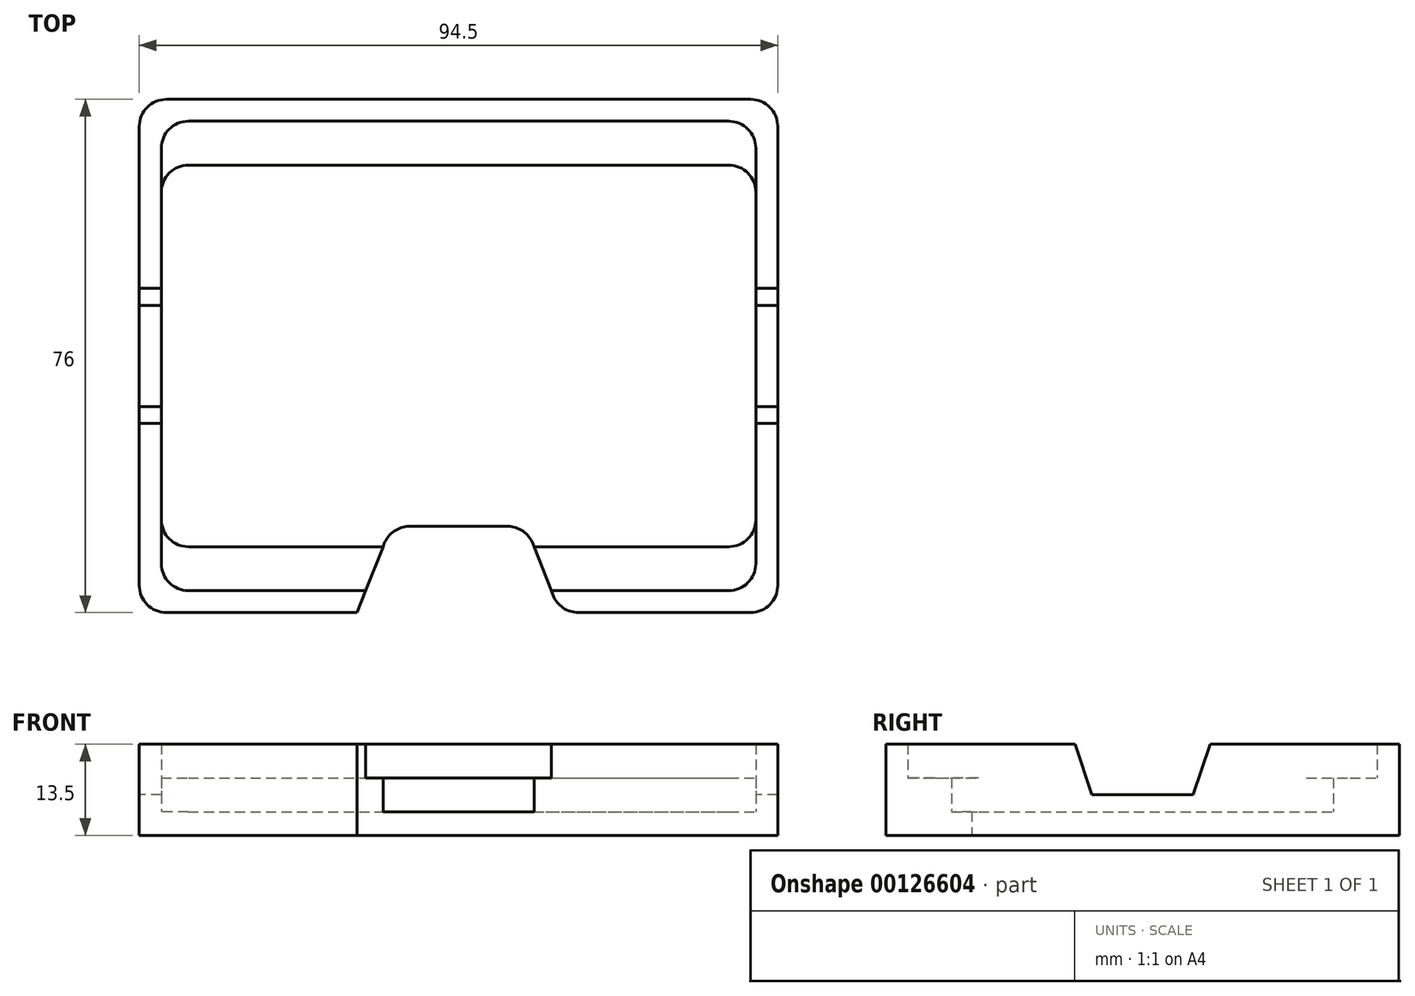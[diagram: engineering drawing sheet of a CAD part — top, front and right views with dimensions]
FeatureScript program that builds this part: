
annotation { "Feature Type Name" : "Feature", "Feature Type Description" : "" }
export const myFeature = defineFeature(function(context is Context, id is Id, definition is map)
    precondition{}
    {
        {
            var Q0;
            Q0=qCreatedBy(makeId("Top.planeOp"),FACE);
            var sketch = newSketch(context, id + "F0", { "sketchPlane" : qUnion([Q0])});
            skLineSegment(sketch, "E0.bottom", {"start": v(4, 0) * mm, "end": v(84, 0) * mm});
            skLineSegment(sketch, "E0.top", {"start": v(4, 56.5) * mm, "end": v(84, 56.5) * mm});
            skLineSegment(sketch, "E0.left", {"start": v(0, 4) * mm, "end": v(0, 52.5) * mm});
            skLineSegment(sketch, "E0.right", {"start": v(88, 4) * mm, "end": v(88, 52.5) * mm});
            skPoint(sketch, "E1.visualSharp", {"position": v(0, 56.5) * mm});
            skArc(sketch, "E1.filletArc", {"start": v(4, 56.5) * mm, "mid": v(1.17, 55.33) * mm, "end": v(0, 52.5) * mm});
            skPoint(sketch, "E2.visualSharp", {"position": v(88, 56.5) * mm});
            skArc(sketch, "E2.filletArc", {"start": v(88, 52.5) * mm, "mid": v(86.83, 55.33) * mm, "end": v(84, 56.5) * mm});
            skPoint(sketch, "E3.visualSharp", {"position": v(88, 0) * mm});
            skArc(sketch, "E3.filletArc", {"start": v(84, 0) * mm, "mid": v(86.83, 1.17) * mm, "end": v(88, 4) * mm});
            skPoint(sketch, "E4.visualSharp", {"position": v(0, 0) * mm});
            skArc(sketch, "E4.filletArc", {"start": v(0, 4) * mm, "mid": v(1.17, 1.17) * mm, "end": v(4, 0) * mm});
            skSolve(sketch);
        }
        {
            var Q0;
            Q0=qCreatedBy(makeId("Top.planeOp"),FACE);
            var sketch = newSketch(context, id + "F1", { "sketchPlane" : qUnion([Q0])});
            skLineSegment(sketch, "E5", {"start": v(0, 0) * mm, "end": v(0, -9.75) * mm, "construction": true});
            skLineSegment(sketch, "E6", {"start": v(0, -9.75) * mm, "end": v(-3.25, -9.75) * mm, "construction": true});
            skLineSegment(sketch, "E7.bottom", {"start": v(0.75, -9.75) * mm, "end": v(87.25, -9.75) * mm});
            skLineSegment(sketch, "E7.top", {"start": v(0.75, 66.25) * mm, "end": v(87.25, 66.25) * mm});
            skLineSegment(sketch, "E7.left", {"start": v(-3.25, -5.75) * mm, "end": v(-3.25, 62.25) * mm});
            skLineSegment(sketch, "E7.right", {"start": v(91.25, -5.75) * mm, "end": v(91.25, 62.25) * mm});
            skPoint(sketch, "E8.0", {"position": v(88, 56.5) * mm});
            skLineSegment(sketch, "E9", {"start": v(88, 56.5) * mm, "end": v(88, 66.25) * mm, "construction": true});
            skLineSegment(sketch, "E10", {"start": v(88, 66.25) * mm, "end": v(91.25, 66.25) * mm, "construction": true});
            skPoint(sketch, "E11.visualSharp", {"position": v(-3.25, 66.25) * mm});
            skArc(sketch, "E11.filletArc", {"start": v(0.75, 66.25) * mm, "mid": v(-2.08, 65.08) * mm, "end": v(-3.25, 62.25) * mm});
            skPoint(sketch, "E12.visualSharp", {"position": v(91.25, 66.25) * mm});
            skArc(sketch, "E12.filletArc", {"start": v(91.25, 62.25) * mm, "mid": v(90.08, 65.08) * mm, "end": v(87.25, 66.25) * mm});
            skPoint(sketch, "E13.visualSharp", {"position": v(91.25, -9.75) * mm});
            skArc(sketch, "E13.filletArc", {"start": v(87.25, -9.75) * mm, "mid": v(90.08, -8.58) * mm, "end": v(91.25, -5.75) * mm});
            skPoint(sketch, "E14.visualSharp", {"position": v(-3.25, -9.75) * mm});
            skArc(sketch, "E14.filletArc", {"start": v(-3.25, -5.75) * mm, "mid": v(-2.08, -8.58) * mm, "end": v(0.75, -9.75) * mm});
            skSolve(sketch);
        }
        {
            var Q0;
            Q0=makeQuery(id+"F1.imprint","IMPRINT",FACE,{"disambiguationData":[TD([[makeQuery(id+"F1.imprint","IMPRINT",EDGE,{"derivedFrom":sQuery(id+"F1.wireOp",EDGE,"E7.bottom")}),1.0]])]});
            extrude(context, id + "F2", {"entities" : qUnion([Q0]), "oppositeDirection" : true, "depth" : 3.5 * mm, "hasSecondDirection" : true, "secondDirectionOppositeDirection" : false, "secondDirectionDepth" : 10 * mm});
        }
        {
            var Q0;
            Q0=makeQuery(id+"F0.imprint","IMPRINT",FACE,{"disambiguationData":[TD([[makeQuery(id+"F0.imprint","IMPRINT",EDGE,{"derivedFrom":sQuery(id+"F0.wireOp",EDGE,"E0.bottom")}),1.0]])]});
            extrude(context, id + "F3", {"entities" : qUnion([Q0]), "operationType" : NewBodyOperationType.REMOVE, "depth" : 5 * mm});
        }
        {
            var Q0;
            Q0=qCreatedBy(makeId("Top.planeOp"),FACE);
            var sketch = newSketch(context, id + "F4", { "sketchPlane" : qUnion([Q0])});
            skLineSegment(sketch, "E15", {"start": v(0, 0) * mm, "end": v(0, -6.5) * mm, "construction": true});
            skLineSegment(sketch, "E16", {"start": v(88, 56.5) * mm, "end": v(88, 63) * mm, "construction": true});
            skLineSegment(sketch, "E17.bottom", {"start": v(4, -6.5) * mm, "end": v(84, -6.5) * mm});
            skLineSegment(sketch, "E17.top", {"start": v(4, 63) * mm, "end": v(84, 63) * mm});
            skLineSegment(sketch, "E17.left", {"start": v(0, -2.5) * mm, "end": v(0, 59) * mm});
            skLineSegment(sketch, "E17.right", {"start": v(88, -2.5) * mm, "end": v(88, 59) * mm});
            skPoint(sketch, "E18.visualSharp", {"position": v(0, 63) * mm});
            skArc(sketch, "E18.filletArc", {"start": v(4, 63) * mm, "mid": v(1.17, 61.83) * mm, "end": v(0, 59) * mm});
            skPoint(sketch, "E19.visualSharp", {"position": v(88, 63) * mm});
            skArc(sketch, "E19.filletArc", {"start": v(88, 59) * mm, "mid": v(86.83, 61.83) * mm, "end": v(84, 63) * mm});
            skPoint(sketch, "E20.visualSharp", {"position": v(88, -6.5) * mm});
            skArc(sketch, "E20.filletArc", {"start": v(84, -6.5) * mm, "mid": v(86.83, -5.33) * mm, "end": v(88, -2.5) * mm});
            skPoint(sketch, "E21.visualSharp", {"position": v(0, -6.5) * mm});
            skArc(sketch, "E21.filletArc", {"start": v(0, -2.5) * mm, "mid": v(1.17, -5.33) * mm, "end": v(4, -6.5) * mm});
            skSolve(sketch);
        }
        {
            var Q0;
            Q0=makeQuery(id+"F4.imprint","IMPRINT",FACE,{"disambiguationData":[TD([[makeQuery(id+"F4.imprint","IMPRINT",EDGE,{"derivedFrom":sQuery(id+"F4.wireOp",EDGE,"E17.bottom")}),1.0]])]});
            extrude(context, id + "F5", {"entities" : qUnion([Q0]), "operationType" : NewBodyOperationType.REMOVE, "depth" : 10 * mm, "hasSecondDirection" : true, "secondDirectionOppositeDirection" : false, "secondDirectionDepth" : 5 * mm});
        }
        {
            var Q0;
            Q0=qCreatedBy(makeId("Top.planeOp"),FACE);
            var sketch = newSketch(context, id + "F6", { "sketchPlane" : qUnion([Q0])});
            skLineSegment(sketch, "E22.0", {"start": v(0.75, -9.75) * mm, "end": v(87.25, -9.75) * mm});
            skLineSegment(sketch, "E23", {"start": v(44, -9.75) * mm, "end": v(44, 3) * mm, "construction": true});
            skLineSegment(sketch, "E24", {"start": v(44, 3) * mm, "end": v(51.27, 3) * mm});
            skLineSegment(sketch, "E25", {"start": v(44, -9.75) * mm, "end": v(59, -9.75) * mm});
            skLineSegment(sketch, "E26", {"start": v(55, 0.46) * mm, "end": v(59, -9.75) * mm});
            skLineSegment(sketch, "E27.MirrorCS", {"start": v(44, -9.75) * mm, "end": v(29, -9.75) * mm});
            skLineSegment(sketch, "E28.MirrorCS", {"start": v(44, 3) * mm, "end": v(36.73, 3) * mm});
            skLineSegment(sketch, "E29.MirrorCS", {"start": v(33, 0.46) * mm, "end": v(29, -9.75) * mm});
            skPoint(sketch, "E30.visualSharp", {"position": v(34, 3) * mm});
            skArc(sketch, "E30.filletArc", {"start": v(36.73, 3) * mm, "mid": v(34.47, 2.3) * mm, "end": v(33, 0.46) * mm});
            skPoint(sketch, "E31.visualSharp", {"position": v(54, 3) * mm});
            skArc(sketch, "E31.filletArc", {"start": v(55, 0.46) * mm, "mid": v(53.53, 2.3) * mm, "end": v(51.27, 3) * mm});
            skSolve(sketch);
        }
        {
            var Q0;
            Q0=makeQuery(id+"F6.imprint","IMPRINT",FACE,{"disambiguationData":[TD([[makeQuery(id+"F6.imprint","IMPRINT",EDGE,{"derivedFrom":sQuery(id+"F6.wireOp",EDGE,"E24")}),-1.0]])]});
            extrude(context, id + "F7", {"entities" : qUnion([Q0]), "operationType" : NewBodyOperationType.REMOVE, "depth" : 10 * mm, "hasSecondDirection" : true, "secondDirectionOppositeDirection" : true, "secondDirectionDepth" : 3.5 * mm});
        }
        {
            var Q0;
            Q0=makeQuery(id+"F7.boolean.opBoolean","COPY",EDGE,{"derivedFrom":makeQuery(id+"F7.opExtrude","SWEPT_EDGE",EDGE,{"disambiguationData":[OSD([sQuery(id+"F6.wireOp",EDGE,"E25"),sQuery(id+"F6.wireOp",EDGE,"E26")])]})});
            var Q1;
            Q1=makeQuery(id+"F7.boolean.opBoolean","COPY",EDGE,{"derivedFrom":makeQuery(id+"F7.opExtrude","SWEPT_EDGE",EDGE,{"disambiguationData":[OSD([sQuery(id+"F6.wireOp",EDGE,"E27.MirrorCS"),sQuery(id+"F6.wireOp",EDGE,"E29.MirrorCS")])]})});
            fillet(context, id + "F8", {"entities" : qUnion([Q0, Q1]), "radius" : 4 * mm, "tangentPropagation" : true, "allowEdgeOverflow" : false});
        }
        {
            var Q0;
            Q0=makeQuery(id+"F2.opExtrude","SWEPT_FACE",FACE,{"disambiguationData":[OSD([sQuery(id+"F1.wireOp",EDGE,"E7.left")])]});
            var sketch = newSketch(context, id + "F9", { "sketchPlane" : qUnion([Q0])});
            skLineSegment(sketch, "E32.0", {"start": v(5.75, 10) * mm, "end": v(-62.25, 10) * mm});
            skLineSegment(sketch, "E33", {"start": v(-28.25, 10) * mm, "end": v(-28.25, 2.5) * mm, "construction": true});
            skPoint(sketch, "E33.endSnap0", {"position": v(-28.25, 10) * mm});
            skLineSegment(sketch, "E34", {"start": v(-28.25, 2.5) * mm, "end": v(-20.75, 2.5) * mm});
            skLineSegment(sketch, "E35", {"start": v(-28.25, 10) * mm, "end": v(-18.25, 10) * mm});
            skLineSegment(sketch, "E36", {"start": v(-18.25, 10) * mm, "end": v(-20.75, 2.5) * mm});
            skLineSegment(sketch, "E37", {"start": v(-18.25, 10) * mm, "end": v(-28.25, 10) * mm});
            skLineSegment(sketch, "E38.MirrorCS", {"start": v(-28.25, 10) * mm, "end": v(-38.25, 10) * mm});
            skLineSegment(sketch, "E39.MirrorCS", {"start": v(-38.25, 10) * mm, "end": v(-28.25, 10) * mm});
            skLineSegment(sketch, "E40.MirrorCS", {"start": v(-38.25, 10) * mm, "end": v(-35.75, 2.5) * mm});
            skLineSegment(sketch, "E41.MirrorCS", {"start": v(-28.25, 2.5) * mm, "end": v(-35.75, 2.5) * mm});
            skSolve(sketch);
        }
        {
            var Q0;
            Q0=makeQuery(id+"F9.imprint","IMPRINT",FACE,{"disambiguationData":[TD([[makeQuery(id+"F9.imprint","IMPRINT",EDGE,{"derivedFrom":sQuery(id+"F9.wireOp",EDGE,"E34")}),1.0]])]});
            extrude(context, id + "F10", {"entities" : qUnion([Q0]), "operationType" : NewBodyOperationType.REMOVE, "endBound" : BoundingType.THROUGH_ALL, "oppositeDirection" : true, "depth" : 25 * mm});
        }
    });
